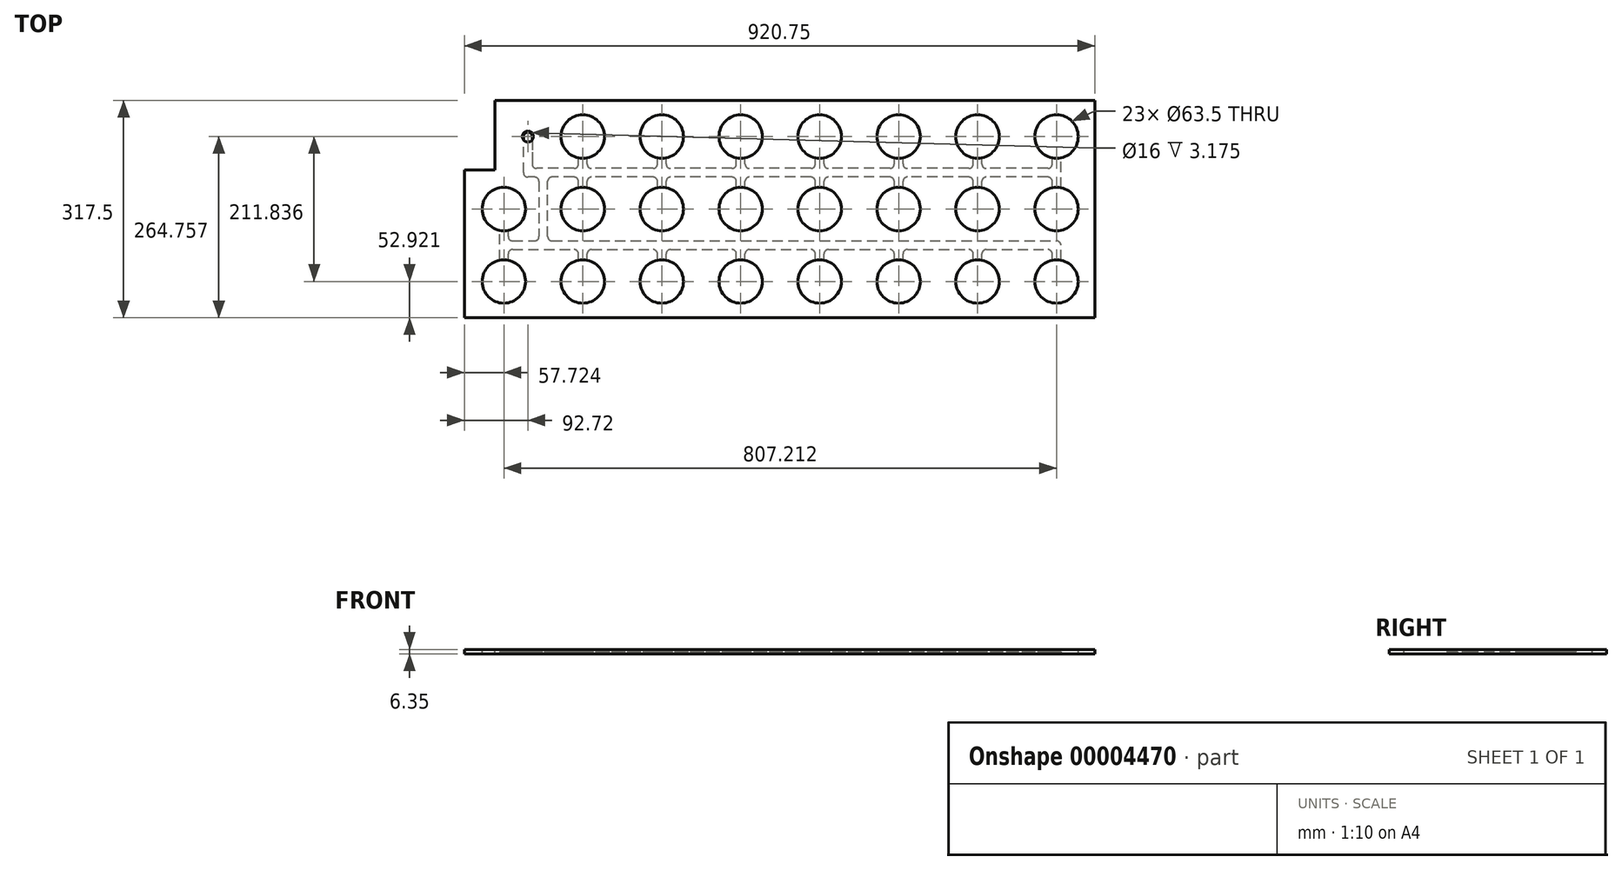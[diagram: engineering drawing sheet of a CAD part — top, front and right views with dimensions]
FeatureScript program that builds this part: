
annotation { "Feature Type Name" : "Feature", "Feature Type Description" : "" }
export const myFeature = defineFeature(function(context is Context, id is Id, definition is map)
    precondition{}
    {
        {
            var Q0;
            Q0=qCreatedBy(makeId("Top.planeOp"),FACE);
            var sketch = newSketch(context, id + "F0", { "sketchPlane" : qUnion([Q0])});
            skLineSegment(sketch, "E0", {"start": v(0, 0) * mm, "end": v(904.88, 0) * mm});
            skLineSegment(sketch, "E1", {"start": v(904.88, 0) * mm, "end": v(904.88, 301.62) * mm});
            skLineSegment(sketch, "E2", {"start": v(904.88, 301.63) * mm, "end": v(44.45, 301.63) * mm});
            skLineSegment(sketch, "E3", {"start": v(44.45, 301.62) * mm, "end": v(44.45, 200.02) * mm});
            skLineSegment(sketch, "E4", {"start": v(44.45, 200.02) * mm, "end": v(0, 200.02) * mm});
            skLineSegment(sketch, "E5", {"start": v(0, 200.02) * mm, "end": v(0, 0) * mm});
            skSolve(sketch);
        }
        {
            var Q0;
            Q0 = qSketchRegion(id + "F0", true);
            extrude(context, id + "F1", {"entities" : qUnion([Q0]), "depth" : 6.35 * mm});
        }
        {
            var Q0;
            Q0=makeQuery(id+"F1.opExtrude","CAP_FACE",FACE,{"disambiguationData":[OSD([sQuery(id+"F0.wireOp",EDGE,"E0"),sQuery(id+"F0.wireOp",EDGE,"E1"),sQuery(id+"F0.wireOp",EDGE,"E2"),sQuery(id+"F0.wireOp",EDGE,"E3"),sQuery(id+"F0.wireOp",EDGE,"E4"),sQuery(id+"F0.wireOp",EDGE,"E5")])],"isStart":false});
            var sketch = newSketch(context, id + "F2", { "sketchPlane" : qUnion([Q0])});
            skCircle(sketch, "E6", {"center": v(49.78, 44.98) * mm, "radius": 31.75 * mm});
            skCircle(sketch, "E7.0.1.0", {"center": v(49.78, 150.9) * mm, "radius": 31.75 * mm});
            skCircle(sketch, "E7.1.0.0", {"center": v(165.1, 44.98) * mm, "radius": 31.75 * mm});
            skCircle(sketch, "E7.1.1.0", {"center": v(165.1, 150.9) * mm, "radius": 31.75 * mm});
            skCircle(sketch, "E7.1.2.0", {"center": v(165.1, 256.82) * mm, "radius": 31.75 * mm});
            skCircle(sketch, "E7.2.0.0", {"center": v(280.42, 44.98) * mm, "radius": 31.75 * mm});
            skCircle(sketch, "E7.2.1.0", {"center": v(280.42, 150.9) * mm, "radius": 31.75 * mm});
            skCircle(sketch, "E7.2.2.0", {"center": v(280.42, 256.82) * mm, "radius": 31.75 * mm});
            skCircle(sketch, "E7.3.0.0", {"center": v(395.73, 44.98) * mm, "radius": 31.75 * mm});
            skCircle(sketch, "E7.3.1.0", {"center": v(395.73, 150.9) * mm, "radius": 31.75 * mm});
            skCircle(sketch, "E7.3.2.0", {"center": v(395.73, 256.82) * mm, "radius": 31.75 * mm});
            skCircle(sketch, "E7.4.0.0", {"center": v(511.05, 44.98) * mm, "radius": 31.75 * mm});
            skCircle(sketch, "E7.4.1.0", {"center": v(511.05, 150.9) * mm, "radius": 31.75 * mm});
            skCircle(sketch, "E7.4.2.0", {"center": v(511.05, 256.82) * mm, "radius": 31.75 * mm});
            skCircle(sketch, "E7.5.0.0", {"center": v(626.36, 44.98) * mm, "radius": 31.75 * mm});
            skCircle(sketch, "E7.5.1.0", {"center": v(626.36, 150.9) * mm, "radius": 31.75 * mm});
            skCircle(sketch, "E7.5.2.0", {"center": v(626.36, 256.82) * mm, "radius": 31.75 * mm});
            skCircle(sketch, "E7.6.0.0", {"center": v(741.68, 44.98) * mm, "radius": 31.75 * mm});
            skCircle(sketch, "E7.6.1.0", {"center": v(741.68, 150.9) * mm, "radius": 31.75 * mm});
            skCircle(sketch, "E7.6.2.0", {"center": v(741.68, 256.82) * mm, "radius": 31.75 * mm});
            skCircle(sketch, "E7.7.0.0", {"center": v(857, 44.98) * mm, "radius": 31.75 * mm});
            skCircle(sketch, "E7.7.1.0", {"center": v(857, 150.9) * mm, "radius": 31.75 * mm});
            skCircle(sketch, "E7.7.2.0", {"center": v(857, 256.82) * mm, "radius": 31.75 * mm});
            skLineSegment(sketch, "E7.direction1", {"start": v(49.78, 44.98) * mm, "end": v(165.1, 44.98) * mm, "construction": true});
            skLineSegment(sketch, "E7.direction2", {"start": v(49.78, 44.98) * mm, "end": v(49.78, 150.9) * mm, "construction": true});
            skCircle(sketch, "E8", {"center": v(84.78, 256.82) * mm, "radius": 8 * mm});
            skSolve(sketch);
        }
        {
            var Q0;
            Q0 = qSketchRegion(id + "F2", true);
            extrude(context, id + "F3", {"entities" : qUnion([Q0]), "operationType" : NewBodyOperationType.REMOVE, "endBound" : BoundingType.THROUGH_ALL, "oppositeDirection" : true, "depth" : 25.4 * mm});
        }
        {
            var Q0;
            Q0=makeQuery(id+"F1.opExtrude","CAP_FACE",FACE,{"disambiguationData":[OSD([sQuery(id+"F0.wireOp",EDGE,"E0"),sQuery(id+"F0.wireOp",EDGE,"E1"),sQuery(id+"F0.wireOp",EDGE,"E2"),sQuery(id+"F0.wireOp",EDGE,"E3"),sQuery(id+"F0.wireOp",EDGE,"E4"),sQuery(id+"F0.wireOp",EDGE,"E5")])],"isStart":true});
            var sketch = newSketch(context, id + "F4", { "sketchPlane" : qUnion([Q0])});
            skLineSegment(sketch, "E9", {"start": v(165.1, -150.9) * mm, "end": v(165.1, -256.82) * mm, "construction": true});
            skLineSegment(sketch, "E10", {"start": v(84.78, -256.82) * mm, "end": v(84.78, -203.86) * mm, "construction": true});
            skLineSegment(sketch, "E11", {"start": v(857, -203.86) * mm, "end": v(84.78, -203.86) * mm, "construction": true});
            skLineSegment(sketch, "E12", {"start": v(107.44, -197.5) * mm, "end": v(107.44, -104.29) * mm, "construction": true});
            skLineSegment(sketch, "E13.0", {"start": v(62.48, -104.29) * mm, "end": v(94.74, -104.29) * mm});
            skLineSegment(sketch, "E14.0", {"start": v(844.3, -197.5) * mm, "end": v(754.38, -197.5) * mm});
            skLineSegment(sketch, "E15.0", {"start": v(91.13, -256.82) * mm, "end": v(91.13, -216.56) * mm});
            skLineSegment(sketch, "E16.0", {"start": v(844.3, -210.2) * mm, "end": v(754.38, -210.2) * mm});
            skLineSegment(sketch, "E17.0", {"start": v(-6.35, -206.37) * mm, "end": v(-6.35, 6.35) * mm});
            skLineSegment(sketch, "E17.1", {"start": v(38.1, -206.37) * mm, "end": v(-6.35, -206.37) * mm});
            skLineSegment(sketch, "E17.2", {"start": v(38.1, -307.98) * mm, "end": v(38.1, -206.37) * mm});
            skLineSegment(sketch, "E17.3", {"start": v(911.23, -307.98) * mm, "end": v(38.1, -307.98) * mm});
            skLineSegment(sketch, "E17.4", {"start": v(911.23, 6.35) * mm, "end": v(911.23, -307.98) * mm});
            skLineSegment(sketch, "E17.5", {"start": v(-6.35, 6.35) * mm, "end": v(911.22, 6.35) * mm});
            skLineSegment(sketch, "E18.0", {"start": v(62.48, -91.59) * mm, "end": v(152.4, -91.59) * mm});
            skLineSegment(sketch, "E19.0", {"start": v(101.1, -191.16) * mm, "end": v(101.1, -110.64) * mm});
            skPoint(sketch, "E20.start.orphan", {"position": v(165.1, -44.98) * mm});
            skLineSegment(sketch, "E21", {"start": v(86.8, -197.5) * mm, "end": v(84.78, -197.5) * mm});
            skLineSegment(sketch, "E22.0", {"start": v(158.75, -44.98) * mm, "end": v(158.75, -85.24) * mm});
            skLineSegment(sketch, "E23.0", {"start": v(43.43, -44.98) * mm, "end": v(43.43, -150.9) * mm});
            skLineSegment(sketch, "E24.0", {"start": v(56.13, -44.98) * mm, "end": v(56.13, -85.24) * mm});
            skLineSegment(sketch, "E25.0", {"start": v(171.45, -44.98) * mm, "end": v(171.45, -85.24) * mm});
            skLineSegment(sketch, "E26", {"start": v(158.75, -44.98) * mm, "end": v(171.45, -44.98) * mm});
            skLineSegment(sketch, "E27.0", {"start": v(171.45, -150.9) * mm, "end": v(171.45, -191.16) * mm});
            skLineSegment(sketch, "E28.0", {"start": v(158.75, -150.9) * mm, "end": v(158.75, -191.16) * mm});
            skLineSegment(sketch, "E29", {"start": v(158.75, -256.82) * mm, "end": v(171.45, -256.82) * mm});
            skLineSegment(sketch, "E30", {"start": v(158.75, -150.9) * mm, "end": v(171.45, -150.9) * mm});
            skLineSegment(sketch, "E31.trimOffspring", {"start": v(171.45, -216.56) * mm, "end": v(171.45, -256.82) * mm});
            skLineSegment(sketch, "E32.trimOffspring", {"start": v(152.4, -197.5) * mm, "end": v(120.14, -197.5) * mm});
            skLineSegment(sketch, "E33.trimOffspring", {"start": v(152.4, -210.2) * mm, "end": v(97.48, -210.2) * mm});
            skLineSegment(sketch, "E34.1.0.0", {"start": v(274.07, -44.98) * mm, "end": v(274.07, -85.24) * mm});
            skLineSegment(sketch, "E34.1.0.1", {"start": v(286.77, -44.98) * mm, "end": v(286.77, -85.24) * mm});
            skLineSegment(sketch, "E34.1.0.2", {"start": v(274.07, -44.98) * mm, "end": v(286.77, -44.98) * mm});
            skLineSegment(sketch, "E34.1.0.3", {"start": v(274.07, -150.9) * mm, "end": v(274.07, -191.16) * mm});
            skLineSegment(sketch, "E34.1.0.4", {"start": v(286.77, -150.9) * mm, "end": v(286.77, -191.16) * mm});
            skLineSegment(sketch, "E34.1.0.5", {"start": v(274.07, -150.9) * mm, "end": v(286.77, -150.9) * mm});
            skLineSegment(sketch, "E34.1.0.6", {"start": v(274.07, -216.56) * mm, "end": v(274.07, -256.82) * mm});
            skLineSegment(sketch, "E34.1.0.7", {"start": v(286.77, -216.56) * mm, "end": v(286.77, -256.82) * mm});
            skLineSegment(sketch, "E34.1.0.8", {"start": v(274.07, -256.82) * mm, "end": v(286.77, -256.82) * mm});
            skLineSegment(sketch, "E34.2.0.0", {"start": v(389.38, -44.98) * mm, "end": v(389.38, -85.24) * mm});
            skLineSegment(sketch, "E34.2.0.1", {"start": v(402.08, -44.98) * mm, "end": v(402.08, -85.24) * mm});
            skLineSegment(sketch, "E34.2.0.2", {"start": v(389.38, -44.98) * mm, "end": v(402.08, -44.98) * mm});
            skLineSegment(sketch, "E34.2.0.3", {"start": v(389.38, -150.9) * mm, "end": v(389.38, -191.16) * mm});
            skLineSegment(sketch, "E34.2.0.4", {"start": v(402.08, -150.9) * mm, "end": v(402.08, -191.16) * mm});
            skLineSegment(sketch, "E34.2.0.5", {"start": v(389.38, -150.9) * mm, "end": v(402.08, -150.9) * mm});
            skLineSegment(sketch, "E34.2.0.6", {"start": v(389.38, -216.56) * mm, "end": v(389.38, -256.82) * mm});
            skLineSegment(sketch, "E34.2.0.7", {"start": v(402.08, -216.56) * mm, "end": v(402.08, -256.82) * mm});
            skLineSegment(sketch, "E34.2.0.8", {"start": v(389.38, -256.82) * mm, "end": v(402.08, -256.82) * mm});
            skLineSegment(sketch, "E34.3.0.0", {"start": v(504.7, -44.98) * mm, "end": v(504.7, -85.24) * mm});
            skLineSegment(sketch, "E34.3.0.1", {"start": v(517.4, -44.98) * mm, "end": v(517.4, -85.24) * mm});
            skLineSegment(sketch, "E34.3.0.2", {"start": v(504.7, -44.98) * mm, "end": v(517.4, -44.98) * mm});
            skLineSegment(sketch, "E34.3.0.3", {"start": v(504.7, -150.9) * mm, "end": v(504.7, -191.16) * mm});
            skLineSegment(sketch, "E34.3.0.4", {"start": v(517.4, -150.9) * mm, "end": v(517.4, -191.16) * mm});
            skLineSegment(sketch, "E34.3.0.5", {"start": v(504.7, -150.9) * mm, "end": v(517.4, -150.9) * mm});
            skLineSegment(sketch, "E34.3.0.6", {"start": v(504.7, -216.56) * mm, "end": v(504.7, -256.82) * mm});
            skLineSegment(sketch, "E34.3.0.7", {"start": v(517.4, -216.56) * mm, "end": v(517.4, -256.82) * mm});
            skLineSegment(sketch, "E34.3.0.8", {"start": v(504.7, -256.82) * mm, "end": v(517.4, -256.82) * mm});
            skLineSegment(sketch, "E34.4.0.0", {"start": v(620.01, -44.98) * mm, "end": v(620.01, -85.24) * mm});
            skLineSegment(sketch, "E34.4.0.1", {"start": v(632.71, -44.98) * mm, "end": v(632.71, -85.24) * mm});
            skLineSegment(sketch, "E34.4.0.2", {"start": v(620.01, -44.98) * mm, "end": v(632.71, -44.98) * mm});
            skLineSegment(sketch, "E34.4.0.3", {"start": v(620.01, -150.9) * mm, "end": v(620.01, -191.16) * mm});
            skLineSegment(sketch, "E34.4.0.4", {"start": v(632.71, -150.9) * mm, "end": v(632.71, -191.16) * mm});
            skLineSegment(sketch, "E34.4.0.5", {"start": v(620.01, -150.9) * mm, "end": v(632.71, -150.9) * mm});
            skLineSegment(sketch, "E34.4.0.6", {"start": v(620.01, -216.56) * mm, "end": v(620.01, -256.82) * mm});
            skLineSegment(sketch, "E34.4.0.7", {"start": v(632.71, -216.56) * mm, "end": v(632.71, -256.82) * mm});
            skLineSegment(sketch, "E34.4.0.8", {"start": v(620.01, -256.82) * mm, "end": v(632.71, -256.82) * mm});
            skLineSegment(sketch, "E34.5.0.0", {"start": v(735.33, -44.98) * mm, "end": v(735.33, -85.24) * mm});
            skLineSegment(sketch, "E34.5.0.1", {"start": v(748.03, -44.98) * mm, "end": v(748.03, -85.24) * mm});
            skLineSegment(sketch, "E34.5.0.2", {"start": v(735.33, -44.98) * mm, "end": v(748.03, -44.98) * mm});
            skLineSegment(sketch, "E34.5.0.3", {"start": v(735.33, -150.9) * mm, "end": v(735.33, -191.16) * mm});
            skLineSegment(sketch, "E34.5.0.4", {"start": v(748.03, -150.9) * mm, "end": v(748.03, -191.16) * mm});
            skLineSegment(sketch, "E34.5.0.5", {"start": v(735.33, -150.9) * mm, "end": v(748.03, -150.9) * mm});
            skLineSegment(sketch, "E34.5.0.6", {"start": v(735.33, -216.56) * mm, "end": v(735.33, -256.82) * mm});
            skLineSegment(sketch, "E34.5.0.7", {"start": v(748.03, -216.56) * mm, "end": v(748.03, -256.82) * mm});
            skLineSegment(sketch, "E34.5.0.8", {"start": v(735.33, -256.82) * mm, "end": v(748.03, -256.82) * mm});
            skLineSegment(sketch, "E34.6.0.0", {"start": v(850.65, -44.98) * mm, "end": v(850.65, -85.24) * mm});
            skLineSegment(sketch, "E34.6.0.1", {"start": v(863.35, -44.98) * mm, "end": v(863.35, -97.94) * mm});
            skLineSegment(sketch, "E34.6.0.2", {"start": v(850.65, -44.98) * mm, "end": v(863.35, -44.98) * mm});
            skLineSegment(sketch, "E34.6.0.3", {"start": v(850.65, -150.9) * mm, "end": v(850.65, -191.16) * mm});
            skLineSegment(sketch, "E34.6.0.4", {"start": v(863.35, -150.9) * mm, "end": v(863.35, -197.5) * mm});
            skLineSegment(sketch, "E34.6.0.5", {"start": v(850.65, -150.9) * mm, "end": v(863.35, -150.9) * mm});
            skLineSegment(sketch, "E34.6.0.6", {"start": v(850.65, -216.56) * mm, "end": v(850.65, -256.82) * mm});
            skLineSegment(sketch, "E34.6.0.7", {"start": v(863.35, -210.2) * mm, "end": v(863.35, -256.82) * mm});
            skLineSegment(sketch, "E34.6.0.8", {"start": v(850.65, -256.82) * mm, "end": v(863.35, -256.82) * mm});
            skLineSegment(sketch, "E35", {"start": v(43.43, -150.9) * mm, "end": v(56.13, -150.9) * mm});
            skLineSegment(sketch, "E36", {"start": v(43.43, -44.98) * mm, "end": v(56.13, -44.98) * mm});
            skLineSegment(sketch, "E37.trimOffspring", {"start": v(56.13, -110.64) * mm, "end": v(56.13, -150.9) * mm});
            skLineSegment(sketch, "E38.trimOffspring", {"start": v(177.8, -91.59) * mm, "end": v(267.72, -91.59) * mm});
            skLineSegment(sketch, "E39.trimOffspring", {"start": v(293.12, -91.59) * mm, "end": v(383.03, -91.59) * mm});
            skLineSegment(sketch, "E40.trimOffspring", {"start": v(408.43, -91.59) * mm, "end": v(498.35, -91.59) * mm});
            skLineSegment(sketch, "E41.trimOffspring", {"start": v(523.75, -91.59) * mm, "end": v(613.66, -91.59) * mm});
            skLineSegment(sketch, "E42.trimOffspring", {"start": v(613.66, -197.5) * mm, "end": v(523.75, -197.5) * mm});
            skLineSegment(sketch, "E43.trimOffspring", {"start": v(613.66, -210.2) * mm, "end": v(523.75, -210.2) * mm});
            skLineSegment(sketch, "E44.trimOffspring", {"start": v(498.35, -197.5) * mm, "end": v(408.43, -197.5) * mm});
            skLineSegment(sketch, "E45.trimOffspring", {"start": v(498.35, -210.2) * mm, "end": v(408.43, -210.2) * mm});
            skLineSegment(sketch, "E46.trimOffspring", {"start": v(383.03, -197.5) * mm, "end": v(293.12, -197.5) * mm});
            skLineSegment(sketch, "E47.trimOffspring", {"start": v(383.03, -210.2) * mm, "end": v(293.12, -210.2) * mm});
            skLineSegment(sketch, "E48.trimOffspring", {"start": v(267.72, -197.5) * mm, "end": v(177.8, -197.5) * mm});
            skLineSegment(sketch, "E49.trimOffspring", {"start": v(267.72, -210.2) * mm, "end": v(177.8, -210.2) * mm});
            skLineSegment(sketch, "E50.trimOffspring", {"start": v(94.74, -197.5) * mm, "end": v(86.8, -197.5) * mm});
            skLineSegment(sketch, "E51.trimOffspring", {"start": v(754.38, -91.59) * mm, "end": v(844.3, -91.59) * mm});
            skLineSegment(sketch, "E52.trimOffspring", {"start": v(728.98, -210.2) * mm, "end": v(639.06, -210.2) * mm});
            skLineSegment(sketch, "E53.trimOffspring", {"start": v(728.98, -197.5) * mm, "end": v(639.06, -197.5) * mm});
            skLineSegment(sketch, "E54", {"start": v(863.35, -197.5) * mm, "end": v(863.35, -210.2) * mm});
            skLineSegment(sketch, "E55", {"start": v(639.06, -91.59) * mm, "end": v(728.98, -91.59) * mm});
            skLineSegment(sketch, "E56", {"start": v(78.43, -256.82) * mm, "end": v(91.13, -256.82) * mm});
            skPoint(sketch, "E57.visualSharp", {"position": v(91.13, -210.2) * mm});
            skArc(sketch, "E57.filletArc", {"start": v(97.48, -210.2) * mm, "mid": v(92.99, -212.07) * mm, "end": v(91.13, -216.56) * mm});
            skPoint(sketch, "E58.visualSharp", {"position": v(78.43, -197.5) * mm});
            skArc(sketch, "E58.filletArc", {"start": v(84.78, -197.5) * mm, "mid": v(80.29, -199.37) * mm, "end": v(78.43, -203.86) * mm});
            skPoint(sketch, "E59.visualSharp", {"position": v(113.8, -197.5) * mm});
            skArc(sketch, "E59.filletArc", {"start": v(113.8, -191.16) * mm, "mid": v(115.65, -195.65) * mm, "end": v(120.14, -197.5) * mm});
            skPoint(sketch, "E60.visualSharp", {"position": v(101.1, -197.5) * mm});
            skArc(sketch, "E60.filletArc", {"start": v(94.74, -197.5) * mm, "mid": v(99.23, -195.65) * mm, "end": v(101.1, -191.16) * mm});
            skPoint(sketch, "E61.visualSharp", {"position": v(158.75, -197.5) * mm});
            skArc(sketch, "E61.filletArc", {"start": v(152.4, -197.5) * mm, "mid": v(156.9, -195.65) * mm, "end": v(158.75, -191.16) * mm});
            skPoint(sketch, "E62.visualSharp", {"position": v(171.45, -197.5) * mm});
            skArc(sketch, "E62.filletArc", {"start": v(171.45, -191.16) * mm, "mid": v(173.3, -195.65) * mm, "end": v(177.8, -197.5) * mm});
            skPoint(sketch, "E63.visualSharp", {"position": v(171.45, -210.2) * mm});
            skArc(sketch, "E63.filletArc", {"start": v(177.8, -210.2) * mm, "mid": v(173.3, -212.07) * mm, "end": v(171.45, -216.56) * mm});
            skLineSegment(sketch, "E64", {"start": v(158.75, -216.56) * mm, "end": v(158.75, -256.82) * mm});
            skPoint(sketch, "E65.visualSharp", {"position": v(158.75, -210.2) * mm});
            skArc(sketch, "E65.filletArc", {"start": v(158.75, -216.56) * mm, "mid": v(156.9, -212.07) * mm, "end": v(152.4, -210.2) * mm});
            skPoint(sketch, "E66.visualSharp", {"position": v(274.07, -210.2) * mm});
            skArc(sketch, "E66.filletArc", {"start": v(274.07, -216.56) * mm, "mid": v(272.2, -212.07) * mm, "end": v(267.72, -210.2) * mm});
            skPoint(sketch, "E67.visualSharp", {"position": v(286.77, -197.5) * mm});
            skArc(sketch, "E67.filletArc", {"start": v(286.77, -191.16) * mm, "mid": v(288.63, -195.65) * mm, "end": v(293.12, -197.5) * mm});
            skPoint(sketch, "E68.visualSharp", {"position": v(274.07, -197.5) * mm});
            skArc(sketch, "E68.filletArc", {"start": v(267.72, -197.5) * mm, "mid": v(272.2, -195.65) * mm, "end": v(274.07, -191.16) * mm});
            skPoint(sketch, "E69.visualSharp", {"position": v(286.77, -210.2) * mm});
            skArc(sketch, "E69.filletArc", {"start": v(293.12, -210.2) * mm, "mid": v(288.63, -212.07) * mm, "end": v(286.77, -216.56) * mm});
            skPoint(sketch, "E70.visualSharp", {"position": v(389.38, -197.5) * mm});
            skArc(sketch, "E70.filletArc", {"start": v(383.03, -197.5) * mm, "mid": v(387.52, -195.65) * mm, "end": v(389.38, -191.16) * mm});
            skPoint(sketch, "E71.visualSharp", {"position": v(402.08, -197.5) * mm});
            skArc(sketch, "E71.filletArc", {"start": v(402.08, -191.16) * mm, "mid": v(403.94, -195.65) * mm, "end": v(408.43, -197.5) * mm});
            skPoint(sketch, "E72.visualSharp", {"position": v(402.08, -210.2) * mm});
            skArc(sketch, "E72.filletArc", {"start": v(408.43, -210.2) * mm, "mid": v(403.94, -212.07) * mm, "end": v(402.08, -216.56) * mm});
            skPoint(sketch, "E73.visualSharp", {"position": v(389.38, -210.2) * mm});
            skArc(sketch, "E73.filletArc", {"start": v(389.38, -216.56) * mm, "mid": v(387.52, -212.07) * mm, "end": v(383.03, -210.2) * mm});
            skPoint(sketch, "E74.visualSharp", {"position": v(504.7, -210.2) * mm});
            skArc(sketch, "E74.filletArc", {"start": v(504.7, -216.56) * mm, "mid": v(502.84, -212.07) * mm, "end": v(498.35, -210.2) * mm});
            skPoint(sketch, "E75.visualSharp", {"position": v(517.4, -197.5) * mm});
            skArc(sketch, "E75.filletArc", {"start": v(517.4, -191.16) * mm, "mid": v(519.26, -195.65) * mm, "end": v(523.75, -197.5) * mm});
            skPoint(sketch, "E76.visualSharp", {"position": v(517.4, -210.2) * mm});
            skArc(sketch, "E76.filletArc", {"start": v(523.75, -210.2) * mm, "mid": v(519.26, -212.07) * mm, "end": v(517.4, -216.56) * mm});
            skPoint(sketch, "E77.visualSharp", {"position": v(504.7, -197.5) * mm});
            skArc(sketch, "E77.filletArc", {"start": v(498.35, -197.5) * mm, "mid": v(502.84, -195.65) * mm, "end": v(504.7, -191.16) * mm});
            skPoint(sketch, "E78.visualSharp", {"position": v(620.01, -197.5) * mm});
            skArc(sketch, "E78.filletArc", {"start": v(613.66, -197.5) * mm, "mid": v(618.15, -195.65) * mm, "end": v(620.01, -191.16) * mm});
            skPoint(sketch, "E79.visualSharp", {"position": v(632.71, -197.5) * mm});
            skArc(sketch, "E79.filletArc", {"start": v(632.71, -191.16) * mm, "mid": v(634.57, -195.65) * mm, "end": v(639.06, -197.5) * mm});
            skPoint(sketch, "E80.visualSharp", {"position": v(632.71, -210.2) * mm});
            skArc(sketch, "E80.filletArc", {"start": v(639.06, -210.2) * mm, "mid": v(634.57, -212.07) * mm, "end": v(632.71, -216.56) * mm});
            skPoint(sketch, "E81.visualSharp", {"position": v(620.01, -210.2) * mm});
            skArc(sketch, "E81.filletArc", {"start": v(620.01, -216.56) * mm, "mid": v(618.15, -212.07) * mm, "end": v(613.66, -210.2) * mm});
            skPoint(sketch, "E82.visualSharp", {"position": v(735.33, -197.5) * mm});
            skArc(sketch, "E82.filletArc", {"start": v(728.98, -197.5) * mm, "mid": v(733.47, -195.65) * mm, "end": v(735.33, -191.16) * mm});
            skPoint(sketch, "E83.visualSharp", {"position": v(748.03, -197.5) * mm});
            skArc(sketch, "E83.filletArc", {"start": v(748.03, -191.16) * mm, "mid": v(749.89, -195.65) * mm, "end": v(754.38, -197.5) * mm});
            skPoint(sketch, "E84.visualSharp", {"position": v(735.33, -210.2) * mm});
            skArc(sketch, "E84.filletArc", {"start": v(735.33, -216.56) * mm, "mid": v(733.47, -212.07) * mm, "end": v(728.98, -210.2) * mm});
            skPoint(sketch, "E85.visualSharp", {"position": v(748.03, -210.2) * mm});
            skArc(sketch, "E85.filletArc", {"start": v(754.38, -210.2) * mm, "mid": v(749.89, -212.07) * mm, "end": v(748.03, -216.56) * mm});
            skPoint(sketch, "E86.visualSharp", {"position": v(850.65, -210.2) * mm});
            skArc(sketch, "E86.filletArc", {"start": v(850.65, -216.56) * mm, "mid": v(848.79, -212.07) * mm, "end": v(844.3, -210.2) * mm});
            skPoint(sketch, "E87.visualSharp", {"position": v(850.65, -197.5) * mm});
            skArc(sketch, "E87.filletArc", {"start": v(844.3, -197.5) * mm, "mid": v(848.79, -195.65) * mm, "end": v(850.65, -191.16) * mm});
            skPoint(sketch, "E88.visualSharp", {"position": v(850.65, -91.59) * mm});
            skArc(sketch, "E88.filletArc", {"start": v(844.3, -91.59) * mm, "mid": v(848.79, -89.73) * mm, "end": v(850.65, -85.24) * mm});
            skPoint(sketch, "E89.visualSharp", {"position": v(863.35, -104.29) * mm});
            skArc(sketch, "E89.filletArc", {"start": v(857, -104.29) * mm, "mid": v(861.49, -102.43) * mm, "end": v(863.35, -97.94) * mm});
            skPoint(sketch, "E90.visualSharp", {"position": v(748.03, -91.59) * mm});
            skArc(sketch, "E90.filletArc", {"start": v(748.03, -85.24) * mm, "mid": v(749.89, -89.73) * mm, "end": v(754.38, -91.59) * mm});
            skPoint(sketch, "E91.visualSharp", {"position": v(735.33, -91.59) * mm});
            skArc(sketch, "E91.filletArc", {"start": v(728.98, -91.59) * mm, "mid": v(733.47, -89.73) * mm, "end": v(735.33, -85.24) * mm});
            skPoint(sketch, "E92.visualSharp", {"position": v(632.71, -91.59) * mm});
            skArc(sketch, "E92.filletArc", {"start": v(632.71, -85.24) * mm, "mid": v(634.57, -89.73) * mm, "end": v(639.06, -91.59) * mm});
            skPoint(sketch, "E93.visualSharp", {"position": v(620.01, -91.59) * mm});
            skArc(sketch, "E93.filletArc", {"start": v(613.66, -91.59) * mm, "mid": v(618.15, -89.73) * mm, "end": v(620.01, -85.24) * mm});
            skPoint(sketch, "E94.visualSharp", {"position": v(517.4, -91.59) * mm});
            skArc(sketch, "E94.filletArc", {"start": v(517.4, -85.24) * mm, "mid": v(519.26, -89.73) * mm, "end": v(523.75, -91.59) * mm});
            skPoint(sketch, "E95.visualSharp", {"position": v(504.7, -91.59) * mm});
            skArc(sketch, "E95.filletArc", {"start": v(498.35, -91.59) * mm, "mid": v(502.84, -89.73) * mm, "end": v(504.7, -85.24) * mm});
            skPoint(sketch, "E96.visualSharp", {"position": v(402.08, -91.59) * mm});
            skArc(sketch, "E96.filletArc", {"start": v(402.08, -85.24) * mm, "mid": v(403.94, -89.73) * mm, "end": v(408.43, -91.59) * mm});
            skPoint(sketch, "E97.visualSharp", {"position": v(389.38, -91.59) * mm});
            skArc(sketch, "E97.filletArc", {"start": v(383.03, -91.59) * mm, "mid": v(387.52, -89.73) * mm, "end": v(389.38, -85.24) * mm});
            skPoint(sketch, "E98.visualSharp", {"position": v(286.77, -91.59) * mm});
            skArc(sketch, "E98.filletArc", {"start": v(286.77, -85.24) * mm, "mid": v(288.63, -89.73) * mm, "end": v(293.12, -91.59) * mm});
            skPoint(sketch, "E99.visualSharp", {"position": v(274.07, -91.59) * mm});
            skArc(sketch, "E99.filletArc", {"start": v(267.72, -91.59) * mm, "mid": v(272.2, -89.73) * mm, "end": v(274.07, -85.24) * mm});
            skPoint(sketch, "E100.visualSharp", {"position": v(171.45, -91.59) * mm});
            skArc(sketch, "E100.filletArc", {"start": v(171.45, -85.24) * mm, "mid": v(173.3, -89.73) * mm, "end": v(177.8, -91.59) * mm});
            skPoint(sketch, "E101.visualSharp", {"position": v(158.75, -91.59) * mm});
            skArc(sketch, "E101.filletArc", {"start": v(152.4, -91.59) * mm, "mid": v(156.9, -89.73) * mm, "end": v(158.75, -85.24) * mm});
            skPoint(sketch, "E102.visualSharp", {"position": v(56.13, -91.59) * mm});
            skArc(sketch, "E102.filletArc", {"start": v(56.13, -85.24) * mm, "mid": v(58, -89.73) * mm, "end": v(62.48, -91.59) * mm});
            skLineSegment(sketch, "E103", {"start": v(113.8, -110.64) * mm, "end": v(113.8, -191.16) * mm});
            skLineSegment(sketch, "E104", {"start": v(120.14, -104.29) * mm, "end": v(857, -104.29) * mm});
            skPoint(sketch, "E105.visualSharp", {"position": v(113.8, -104.29) * mm});
            skArc(sketch, "E105.filletArc", {"start": v(120.14, -104.29) * mm, "mid": v(115.65, -106.15) * mm, "end": v(113.8, -110.64) * mm});
            skPoint(sketch, "E106.visualSharp", {"position": v(101.1, -104.29) * mm});
            skArc(sketch, "E106.filletArc", {"start": v(101.1, -110.64) * mm, "mid": v(99.23, -106.15) * mm, "end": v(94.74, -104.29) * mm});
            skPoint(sketch, "E107.visualSharp", {"position": v(56.13, -104.29) * mm});
            skArc(sketch, "E107.filletArc", {"start": v(62.48, -104.29) * mm, "mid": v(58, -106.15) * mm, "end": v(56.13, -110.64) * mm});
            skLineSegment(sketch, "E108", {"start": v(78.43, -203.86) * mm, "end": v(78.43, -256.82) * mm});
            skSolve(sketch);
        }
        {
            var Q0;
            Q0=makeQuery(id+"F4.imprint","IMPRINT",FACE,{"disambiguationData":[TD([[makeQuery(id+"F4.imprint","IMPRINT",EDGE,{"derivedFrom":sQuery(id+"F4.wireOp",EDGE,"E13.0")}),1.0]])]});
            extrude(context, id + "F5", {"entities" : qUnion([Q0]), "operationType" : NewBodyOperationType.REMOVE, "oppositeDirection" : true, "depth" : 3.17 * mm});
        }
        {
            var Q0;
            Q0=makeQuery(id+"F1.opExtrude","CAP_FACE",FACE,{"disambiguationData":[OSD([sQuery(id+"F0.wireOp",EDGE,"E0"),sQuery(id+"F0.wireOp",EDGE,"E1"),sQuery(id+"F0.wireOp",EDGE,"E2"),sQuery(id+"F0.wireOp",EDGE,"E3"),sQuery(id+"F0.wireOp",EDGE,"E4"),sQuery(id+"F0.wireOp",EDGE,"E5")])],"isStart":true});
            var sketch = newSketch(context, id + "F6", { "sketchPlane" : qUnion([Q0])});
            skArc(sketch, "E109", {"start": v(78.43, -256.82) * mm, "mid": v(84.78, -263.17) * mm, "end": v(91.13, -256.82) * mm});
            skLineSegment(sketch, "E110", {"start": v(78.43, -251.95) * mm, "end": v(78.43, -256.82) * mm});
            skLineSegment(sketch, "E111", {"start": v(91.13, -256.82) * mm, "end": v(91.13, -251.95) * mm});
            skArc(sketch, "E112", {"start": v(78.43, -251.95) * mm, "mid": v(84.78, -264.82) * mm, "end": v(91.13, -251.95) * mm});
            skSolve(sketch);
        }
        {
            var Q0;
            Q0=makeQuery(id+"F6.imprint","IMPRINT",FACE,{"disambiguationData":[TD([[makeQuery(id+"F6.imprint","IMPRINT",EDGE,{"derivedFrom":sQuery(id+"F6.wireOp",EDGE,"E109")}),-1.0]])]});
            extrude(context, id + "F7", {"entities" : qUnion([Q0]), "operationType" : NewBodyOperationType.ADD, "oppositeDirection" : true, "depth" : 3.17 * mm});
        }
        {
            var Q0;
            Q0=makeQuery(id+"F1.opExtrude","CAP_FACE",FACE,{"disambiguationData":[OSD([sQuery(id+"F0.wireOp",EDGE,"E0"),sQuery(id+"F0.wireOp",EDGE,"E1"),sQuery(id+"F0.wireOp",EDGE,"E2"),sQuery(id+"F0.wireOp",EDGE,"E3"),sQuery(id+"F0.wireOp",EDGE,"E4"),sQuery(id+"F0.wireOp",EDGE,"E5")])],"isStart":false});
            var sketch = newSketch(context, id + "F8", { "sketchPlane" : qUnion([Q0])});
            skLineSegment(sketch, "E113", {"start": v(44.45, 301.62) * mm, "end": v(904.88, 301.63) * mm});
            skLineSegment(sketch, "E114", {"start": v(904.88, 301.63) * mm, "end": v(904.88, 0) * mm});
            skLineSegment(sketch, "E115", {"start": v(904.88, 0) * mm, "end": v(0, 0) * mm});
            skLineSegment(sketch, "E116", {"start": v(0, 0) * mm, "end": v(0, 200.02) * mm});
            skLineSegment(sketch, "E117", {"start": v(0, 200.02) * mm, "end": v(44.45, 200.02) * mm});
            skLineSegment(sketch, "E118", {"start": v(44.45, 200.02) * mm, "end": v(44.45, 301.62) * mm});
            skLineSegment(sketch, "E119.0", {"start": v(36.51, 309.56) * mm, "end": v(912.81, 309.56) * mm});
            skLineSegment(sketch, "E119.1", {"start": v(36.51, 207.96) * mm, "end": v(36.51, 309.56) * mm});
            skLineSegment(sketch, "E119.2", {"start": v(-7.94, 207.96) * mm, "end": v(36.51, 207.96) * mm});
            skLineSegment(sketch, "E119.3", {"start": v(-7.94, -7.94) * mm, "end": v(-7.94, 207.96) * mm});
            skLineSegment(sketch, "E119.4", {"start": v(912.81, -7.94) * mm, "end": v(-7.94, -7.94) * mm});
            skLineSegment(sketch, "E119.5", {"start": v(912.81, 309.56) * mm, "end": v(912.81, -7.94) * mm});
            skSolve(sketch);
        }
        {
            var Q0;
            Q0=makeQuery(id+"F8.imprint","IMPRINT",FACE,{"disambiguationData":[TD([[makeQuery(id+"F8.imprint","IMPRINT",EDGE,{"derivedFrom":sQuery(id+"F8.wireOp",EDGE,"E113")}),-1.0]])]});
            extrude(context, id + "F9", {"entities" : qUnion([Q0]), "operationType" : NewBodyOperationType.ADD, "oppositeDirection" : true, "depth" : 6.35 * mm});
        }
    });
